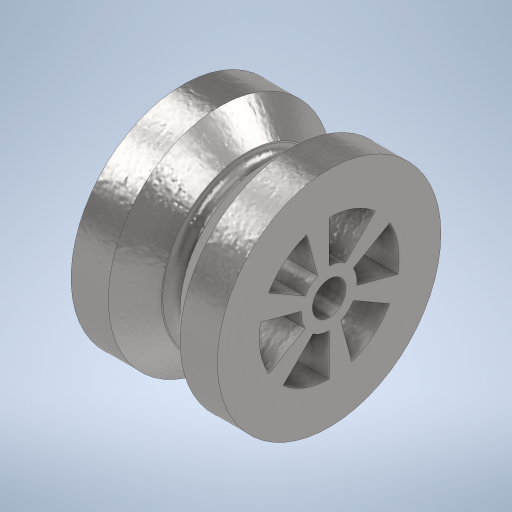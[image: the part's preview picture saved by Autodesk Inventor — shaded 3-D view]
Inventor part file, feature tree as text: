
AUTODESK INVENTOR PART (.ipt)
format: ipt  version: 2024 (Build 280153000, 153)  size: 384,512 bytes
history: native  units: mm
features: sketch x3, extrude x2, revolve x1, pattern_circular x1, projected_geometry x1
ambient origin geometry x8: Origin, YZ Plane, XZ Plane, XY Plane, X Axis, Y Axis, Z Axis, Center Point
bodies: Volumenkörper1 (feature_tree)
feature tree (8):
  revolve  "Umdrehung1"
  extrude  "Extrusion2"  TaperAngle=45.0deg  [1 undecoded]
  pattern_circular  "Runde Anordnung2"  [2 undecoded]
  extrude  "Extrusion3"  Depth=7.85mm
  sketch  "Skizze1"  dims[d0=2.0mm d1=45.0deg]
  sketch  "Skizze2"  dims[d2=0.5mm]
  projected_geometry  "Projizierte Kontur1"
  sketch  "Skizze3"  dims[d3=12.0mm d4=9.0mm d5=7.85mm d6=90.0deg d7=3.0mm d8=45.0deg d9=0.5mm d10=7.5mm d16=0.0mm d17=0.0mm d18=60.0mm d19=360.0deg d21=1.8mm d22=10.0mm d23=0.0mm]
note: 3 required parameter values undecoded (feature->parameter linkage not recoverable at this tier; creation-order binding heuristic only, values carry confidence <= 0.55)
